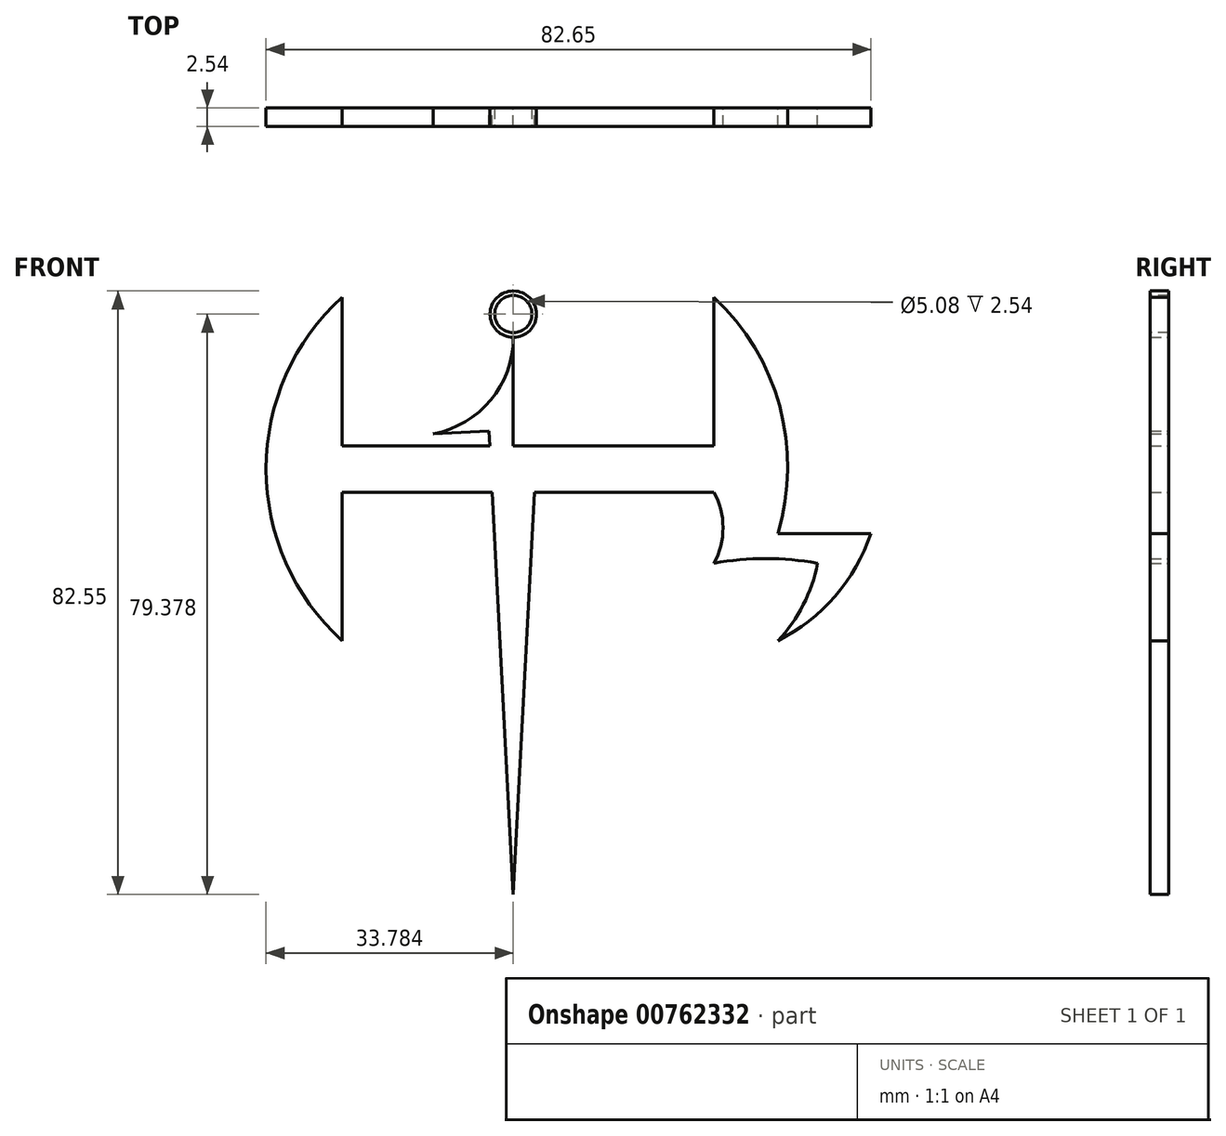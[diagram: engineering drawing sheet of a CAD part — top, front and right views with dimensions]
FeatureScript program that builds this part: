
annotation { "Feature Type Name" : "Feature", "Feature Type Description" : "" }
export const myFeature = defineFeature(function(context is Context, id is Id, definition is map)
    precondition{}
    {
        {
            var Q0;
            Q0=qCreatedBy(makeId("Front.planeOp"),FACE);
            var sketch = newSketch(context, id + "F0", { "sketchPlane" : qUnion([Q0])});
            skLineSegment(sketch, "E0", {"start": v(-16.98, 35) * mm, "end": v(-16.98, -41.2) * mm});
            skLineSegment(sketch, "E1", {"start": v(-16.98, -41.2) * mm, "end": v(-20.3, 22.2) * mm});
            skLineSegment(sketch, "E2", {"start": v(-20.3, 22.2) * mm, "end": v(-27.9, 21.8) * mm});
            skArc(sketch, "E3", {"start": v(-27.9, 21.8) * mm, "mid": v(-20.06, 26.43) * mm, "end": v(-16.98, 35) * mm});
            skArc(sketch, "E4.MirrorCS", {"start": v(-6.04, 21.8) * mm, "mid": v(-13.89, 26.43) * mm, "end": v(-16.98, 35) * mm});
            skLineSegment(sketch, "E5.MirrorCS", {"start": v(-13.65, 22.2) * mm, "end": v(-6.04, 21.8) * mm});
            skLineSegment(sketch, "E6.MirrorCS", {"start": v(-16.98, -41.2) * mm, "end": v(-13.65, 22.2) * mm});
            skLineSegment(sketch, "E7", {"start": v(-40.37, 20.18) * mm, "end": v(10.43, 20.18) * mm});
            skLineSegment(sketch, "E8.0", {"start": v(-40.37, 13.83) * mm, "end": v(10.43, 13.83) * mm});
            skLineSegment(sketch, "E9", {"start": v(-40.37, 20.18) * mm, "end": v(-40.37, 40.5) * mm});
            skLineSegment(sketch, "E10", {"start": v(-40.37, 13.83) * mm, "end": v(-40.37, -6.49) * mm});
            skArc(sketch, "E11", {"start": v(-40.37, 40.5) * mm, "mid": v(-50.76, 17) * mm, "end": v(-40.37, -6.49) * mm});
            skLineSegment(sketch, "E12", {"start": v(10.43, 20.18) * mm, "end": v(10.43, 40.5) * mm});
            skArc(sketch, "E13", {"start": v(19.19, 8.17) * mm, "mid": v(19.42, 25.59) * mm, "end": v(10.43, 40.5) * mm});
            skLineSegment(sketch, "E14", {"start": v(19.19, 8.17) * mm, "end": v(31.89, 8.17) * mm});
            skArc(sketch, "E15", {"start": v(19.19, -6.49) * mm, "mid": v(27, -0.42) * mm, "end": v(31.89, 8.17) * mm});
            skArc(sketch, "E16", {"start": v(19.19, -6.49) * mm, "mid": v(22.65, -1.58) * mm, "end": v(24.6, 4.1) * mm});
            skArc(sketch, "E17", {"start": v(10.43, 4.1) * mm, "mid": v(11.69, 8.96) * mm, "end": v(10.43, 13.83) * mm});
            skArc(sketch, "E18", {"start": v(24.6, 4.1) * mm, "mid": v(17.51, 4.75) * mm, "end": v(10.43, 4.1) * mm});
            skCircle(sketch, "E19", {"center": v(-16.98, 38.17) * mm, "radius": 3.18 * mm});
            skSolve(sketch);
        }
        {
            var Q0;
            {var subQ0=sQuery(id+"F0.wireOp",EDGE,"E9");Q0=makeQuery(id+"F0.imprint","IMPRINT",FACE,{"disambiguationData":[TD([[makeQuery(id+"F0.imprint","IMPRINT",EDGE,{"derivedFrom":subQ0}),1.0]])]});}
            var Q1;
            {var subQ0=sQuery(id+"F0.wireOp",EDGE,"E7");var subQ1=sQuery(id+"F0.wireOp",EDGE,"E0");var subQ2=makeQuery(id+"F0.imprint","INTERSECT",VERTEX,{"derivedFrom":[subQ1,subQ0]});Q1=makeQuery(id+"F0.imprint","IMPRINT",FACE,{"disambiguationData":[TD([[makeQuery(id+"F0.imprint","IMPRINT",EDGE,{"disambiguationData":[TD([[subQ2,-1.0]])],"derivedFrom":subQ1}),-1.0]])]});}
            var Q2;
            {var subQ0=sQuery(id+"F0.wireOp",EDGE,"E7");var subQ1=sQuery(id+"F0.wireOp",EDGE,"E0");var subQ2=makeQuery(id+"F0.imprint","INTERSECT",VERTEX,{"derivedFrom":[subQ1,subQ0]});Q2=makeQuery(id+"F0.imprint","IMPRINT",FACE,{"disambiguationData":[TD([[makeQuery(id+"F0.imprint","IMPRINT",EDGE,{"disambiguationData":[TD([[subQ2,-1.0]])],"derivedFrom":subQ1}),1.0]])]});}
            var Q3;
            {var subQ4=sQuery(id+"F0.wireOp",EDGE,"E4.MirrorCS");Q3=makeQuery(id+"F0.imprint","IMPRINT",FACE,{"disambiguationData":[TD([[makeQuery(id+"F0.imprint","IMPRINT",EDGE,{"derivedFrom":subQ4}),1.0]])]});}
            var Q4;
            {var subQ1=sQuery(id+"F0.wireOp",EDGE,"E2");Q4=makeQuery(id+"F0.imprint","IMPRINT",FACE,{"disambiguationData":[TD([[makeQuery(id+"F0.imprint","IMPRINT",EDGE,{"derivedFrom":subQ1}),-1.0]])]});}
            var Q5;
            {var subQ0=sQuery(id+"F0.wireOp",EDGE,"E1");var subQ3=sQuery(id+"F0.wireOp",EDGE,"E8.0");var subQ5=makeQuery(id+"F0.imprint","INTERSECT",VERTEX,{"derivedFrom":[subQ0,subQ3]});Q5=makeQuery(id+"F0.imprint","IMPRINT",FACE,{"disambiguationData":[TD([[makeQuery(id+"F0.imprint","IMPRINT",EDGE,{"disambiguationData":[TD([[subQ5,-1.0]])],"derivedFrom":subQ3}),-1.0]])]});}
            var Q6;
            {var subQ0=sQuery(id+"F0.wireOp",EDGE,"E6.MirrorCS");var subQ3=sQuery(id+"F0.wireOp",EDGE,"E8.0");var subQ5=makeQuery(id+"F0.imprint","INTERSECT",VERTEX,{"derivedFrom":[subQ0,subQ3]});Q6=makeQuery(id+"F0.imprint","IMPRINT",FACE,{"disambiguationData":[TD([[makeQuery(id+"F0.imprint","IMPRINT",EDGE,{"disambiguationData":[TD([[subQ5,1.0]])],"derivedFrom":subQ3}),-1.0]])]});}
            var Q7;
            {var subQ0=sQuery(id+"F0.wireOp",EDGE,"E12");Q7=makeQuery(id+"F0.imprint","IMPRINT",FACE,{"disambiguationData":[TD([[makeQuery(id+"F0.imprint","IMPRINT",EDGE,{"derivedFrom":subQ0}),-1.0]])]});}
            var Q8;
            Q8=makeQuery(id+"F0.imprint","IMPRINT",FACE,{"disambiguationData":[TD([[makeQuery(id+"F0.imprint","IMPRINT",EDGE,{"derivedFrom":sQuery(id+"F0.wireOp",EDGE,"E19")}),1.0]])]});
            extrude(context, id + "F1", {"entities" : qUnion([Q0, Q1, Q2, Q3, Q4, Q5, Q6, Q7, Q8]), "depth" : 2.54 * mm, "offsetDistance" : 25.4 * mm});
        }
        {
            var Q0;
            Q0=makeQuery(id+"F1.opExtrude","CAP_FACE",FACE,{"disambiguationData":[OSD([sQuery(id+"F0.wireOp",EDGE,"E19")])],"isStart":false});
            var sketch = newSketch(context, id + "F2", { "sketchPlane" : qUnion([Q0])});
            skCircle(sketch, "E20", {"center": v(-16.98, 38.17) * mm, "radius": 2.54 * mm});
            skSolve(sketch);
        }
        {
            var Q0;
            Q0=makeQuery(id+"F2.imprint","IMPRINT",FACE,{"disambiguationData":[TD([[makeQuery(id+"F2.imprint","IMPRINT",EDGE,{"derivedFrom":sQuery(id+"F2.wireOp",EDGE,"E20")}),1.0]])]});
            extrude(context, id + "F3", {"entities" : qUnion([Q0]), "operationType" : NewBodyOperationType.REMOVE, "oppositeDirection" : true, "depth" : 25.4 * mm, "offsetDistance" : 25.4 * mm});
        }
    });
